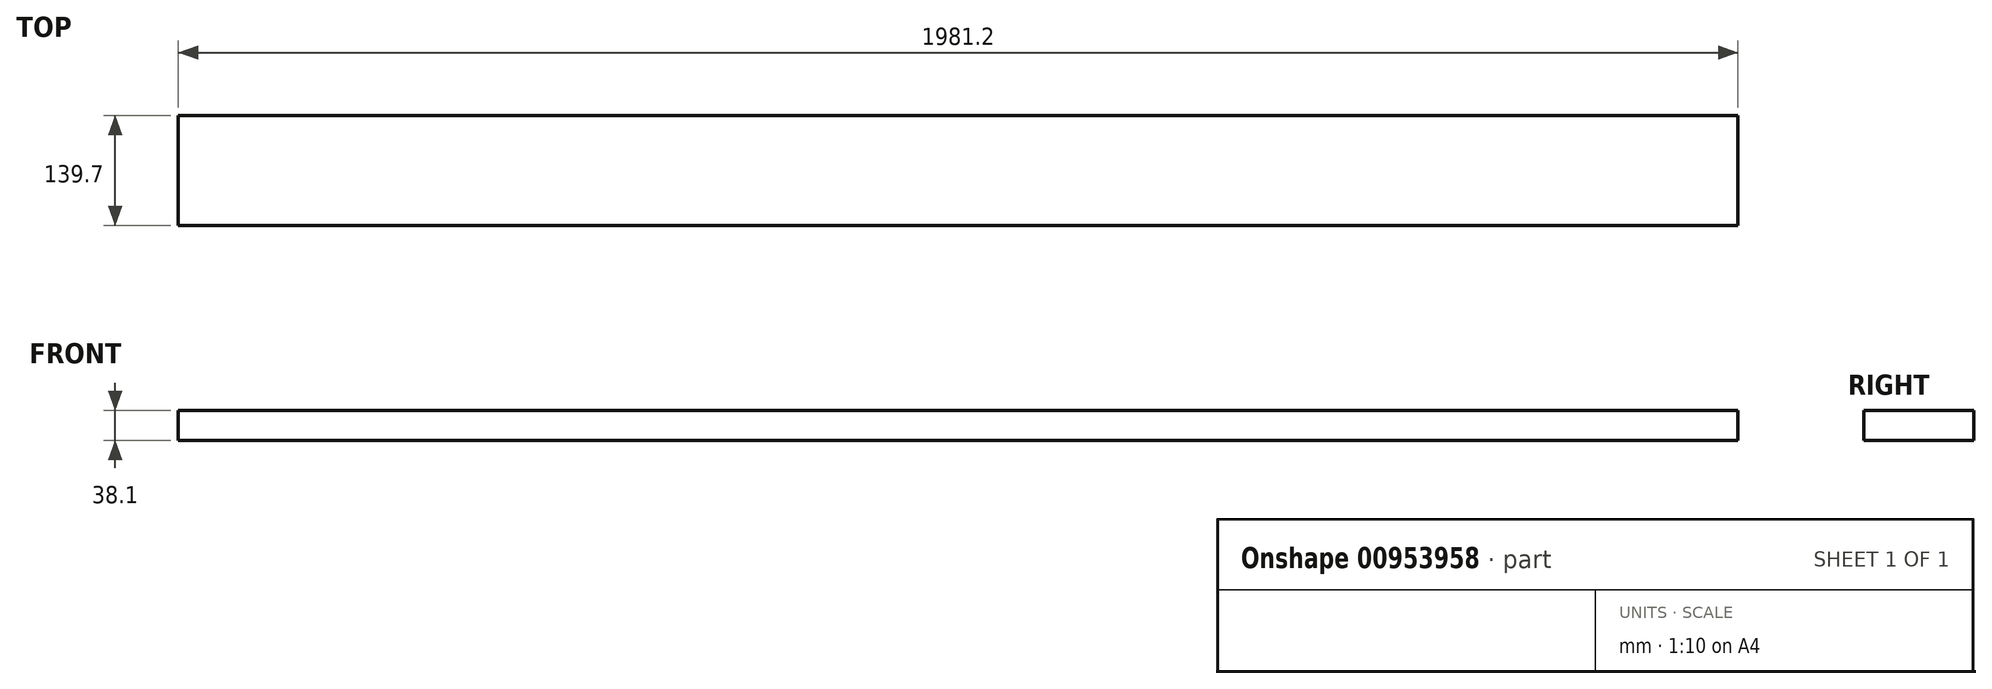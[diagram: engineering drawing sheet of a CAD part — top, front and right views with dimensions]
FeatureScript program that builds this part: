
annotation { "Feature Type Name" : "Feature", "Feature Type Description" : "" }
export const myFeature = defineFeature(function(context is Context, id is Id, definition is map)
    precondition{}
    {
        {
            var Q0;
            Q0=qCreatedBy(makeId("Top.planeOp"),FACE);
            var sketch = newSketch(context, id + "F0", { "sketchPlane" : qUnion([Q0])});
            skLineSegment(sketch, "E0.bottom", {"start": v(0, 0) * mm, "end": v(1981.2, 0) * mm});
            skLineSegment(sketch, "E0.top", {"start": v(0, 139.7) * mm, "end": v(1981.2, 139.7) * mm});
            skLineSegment(sketch, "E0.left", {"start": v(0, 0) * mm, "end": v(0, 139.7) * mm});
            skLineSegment(sketch, "E0.right", {"start": v(1981.2, 0) * mm, "end": v(1981.2, 139.7) * mm});
            skSolve(sketch);
        }
        {
            var Q0;
            Q0=qSketchRegion(id+"F0",true);
            extrude(context, id + "F1", {"entities" : qUnion([Q0]), "depth" : 38.1 * mm, "offsetDistance" : 25.4 * mm});
        }
    });
